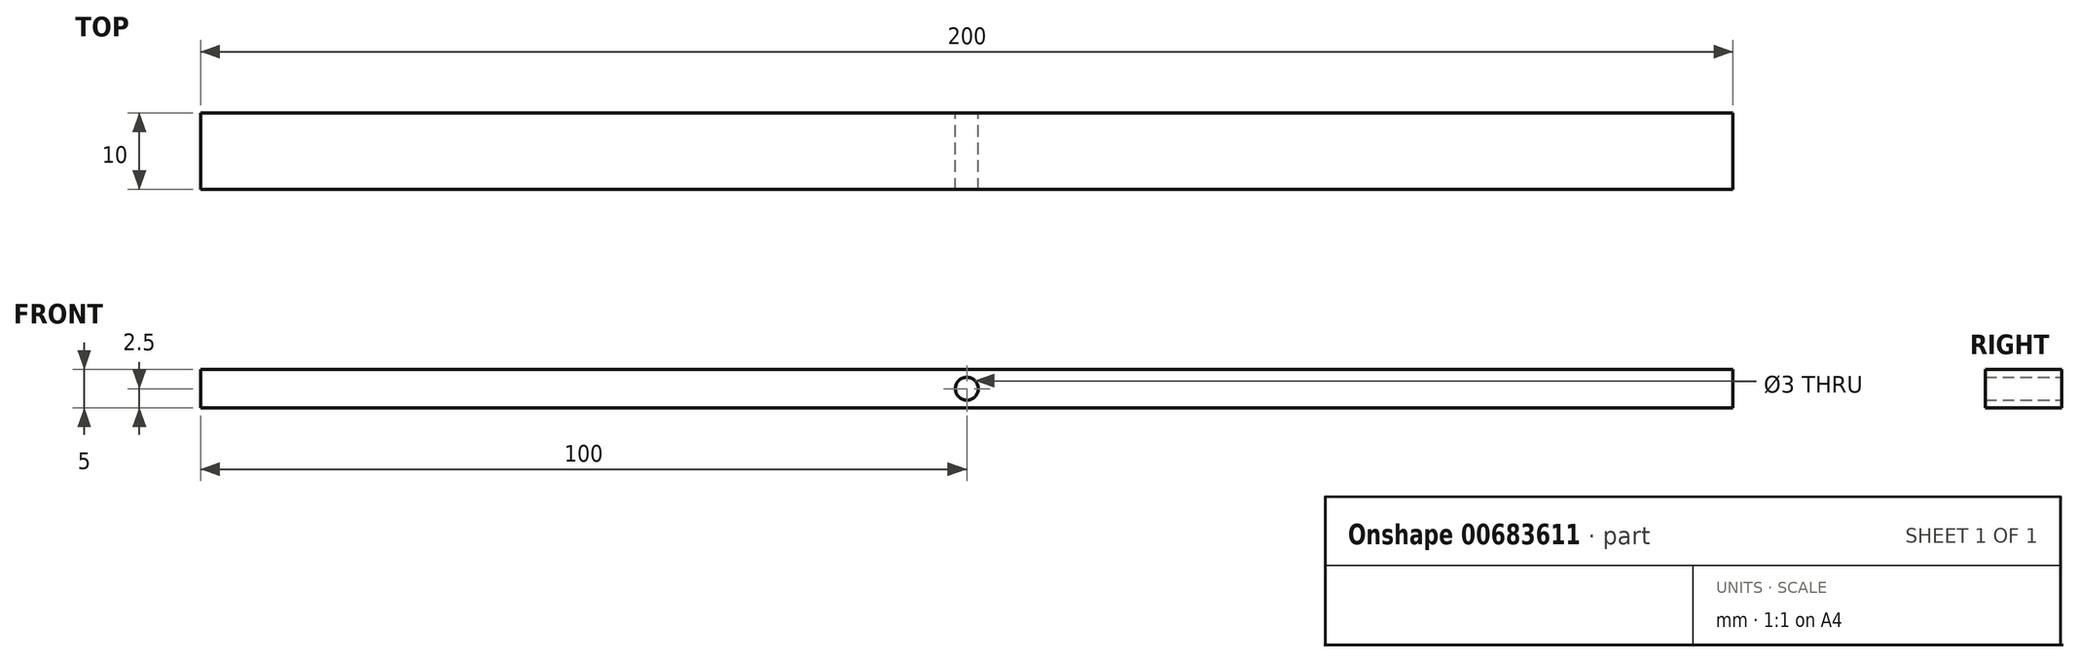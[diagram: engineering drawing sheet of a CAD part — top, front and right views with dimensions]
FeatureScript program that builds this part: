
annotation { "Feature Type Name" : "Feature", "Feature Type Description" : "" }
export const myFeature = defineFeature(function(context is Context, id is Id, definition is map)
    precondition{}
    {
        {
            var Q0;
            Q0=qCreatedBy(makeId("Front.planeOp"),FACE);
            var sketch = newSketch(context, id + "F0", { "sketchPlane" : qUnion([Q0])});
            skLineSegment(sketch, "E0.bottom", {"start": v(100, 2.5) * mm, "end": v(-100, 2.5) * mm});
            skLineSegment(sketch, "E0.top", {"start": v(100, -2.5) * mm, "end": v(-100, -2.5) * mm});
            skLineSegment(sketch, "E0.left", {"start": v(100, 2.5) * mm, "end": v(100, -2.5) * mm});
            skLineSegment(sketch, "E0.right", {"start": v(-100, 2.5) * mm, "end": v(-100, -2.5) * mm});
            skPoint(sketch, "E0.middle", {"position": v(0, 0) * mm});
            skCircle(sketch, "E1", {"center": v(0, 0) * mm, "radius": 1.5 * mm});
            skSolve(sketch);
        }
        {
            var Q0;
            Q0 = qSketchRegion(id + "F0", true);
            extrude(context, id + "F1", {"entities" : qUnion([Q0]), "endBound" : BoundingType.SYMMETRIC, "depth" : 10 * mm, "offsetDistance" : 25 * mm});
        }
    });
